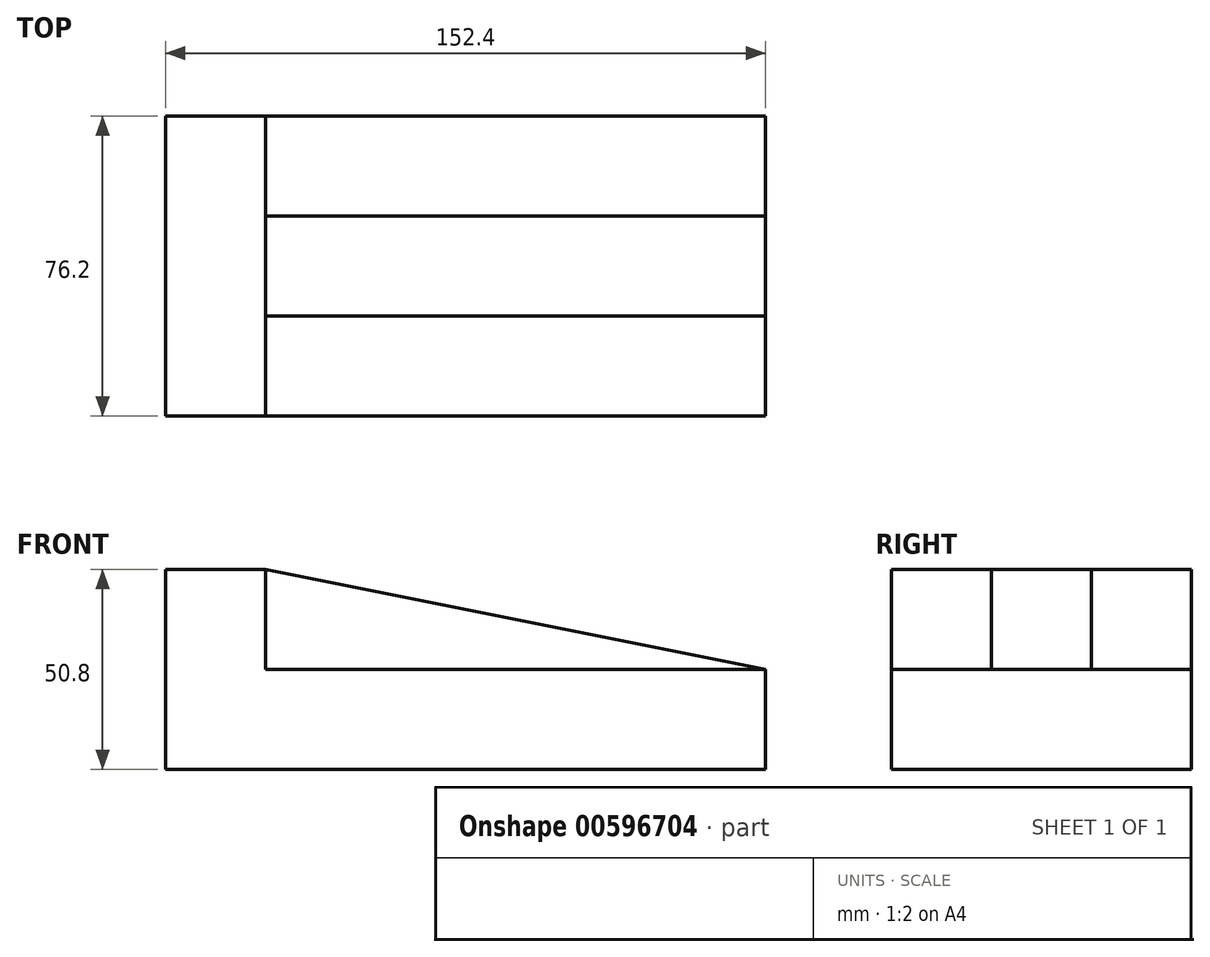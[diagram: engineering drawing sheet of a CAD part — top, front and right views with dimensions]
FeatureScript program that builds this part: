
annotation { "Feature Type Name" : "Feature", "Feature Type Description" : "" }
export const myFeature = defineFeature(function(context is Context, id is Id, definition is map)
    precondition{}
    {
        {
            var Q0;
            Q0=qCreatedBy(makeId("Front.planeOp"),FACE);
            var sketch = newSketch(context, id + "F0", { "sketchPlane" : qUnion([Q0])});
            skLineSegment(sketch, "E0", {"start": v(0, 0) * mm, "end": v(0, 50.8) * mm});
            skLineSegment(sketch, "E1", {"start": v(0, 50.8) * mm, "end": v(25.4, 50.8) * mm});
            skLineSegment(sketch, "E2", {"start": v(0, 0) * mm, "end": v(152.4, 0) * mm});
            skLineSegment(sketch, "E3", {"start": v(152.4, 0) * mm, "end": v(152.4, 25.4) * mm});
            skLineSegment(sketch, "E4", {"start": v(25.4, 50.8) * mm, "end": v(25.4, 25.4) * mm});
            skLineSegment(sketch, "E5", {"start": v(25.4, 25.4) * mm, "end": v(152.4, 25.4) * mm});
            skSolve(sketch);
        }
        {
            var Q0;
            Q0=makeQuery(id+"F0.imprint","IMPRINT",FACE,{"disambiguationData":[TD([[makeQuery(id+"F0.imprint","IMPRINT",EDGE,{"derivedFrom":sQuery(id+"F0.wireOp",EDGE,"E0")}),-1.0]])]});
            extrude(context, id + "F1", {"entities" : qUnion([Q0]), "oppositeDirection" : true, "depth" : 76.2 * mm, "offsetDistance" : 25.4 * mm});
        }
        {
            var Q0;
            Q0=makeQuery(id+"F1.opExtrude","SWEPT_FACE",FACE,{"disambiguationData":[OSD([sQuery(id+"F0.wireOp",EDGE,"E1")])]});
            var sketch = newSketch(context, id + "F2", { "sketchPlane" : qUnion([Q0])});
            skLineSegment(sketch, "E6", {"start": v(25.4, 76.2) * mm, "end": v(25.4, 50.8) * mm});
            skLineSegment(sketch, "E7", {"start": v(25.4, 0) * mm, "end": v(25.4, 25.4) * mm});
            skLineSegment(sketch, "E8", {"start": v(25.4, 25.4) * mm, "end": v(152.4, 25.4) * mm});
            skLineSegment(sketch, "E9", {"start": v(25.4, 50.8) * mm, "end": v(152.4, 50.8) * mm});
            skLineSegment(sketch, "E10", {"start": v(152.4, 50.8) * mm, "end": v(152.4, 25.4) * mm});
            skLineSegment(sketch, "E11", {"start": v(25.4, 50.8) * mm, "end": v(25.4, 25.4) * mm});
            skSolve(sketch);
        }
        {
            var Q0;
            Q0=makeQuery(id+"F2.imprint","IMPRINT",FACE,{"disambiguationData":[TD([[makeQuery(id+"F2.imprint","IMPRINT",EDGE,{"derivedFrom":sQuery(id+"F2.wireOp",EDGE,"E8")}),1.0]])]});
            extrude(context, id + "F3", {"entities" : qUnion([Q0]), "operationType" : NewBodyOperationType.ADD, "oppositeDirection" : true, "depth" : 25.4 * mm, "offsetDistance" : 25.4 * mm});
        }
        {
            var Q0;
            Q0=makeQuery(id+"F3.opExtrude","SWEPT_FACE",FACE,{"disambiguationData":[OSD([sQuery(id+"F2.wireOp",EDGE,"E8")])]});
            var sketch = newSketch(context, id + "F4", { "sketchPlane" : qUnion([Q0])});
            skLineSegment(sketch, "E12", {"start": v(25.4, 50.8) * mm, "end": v(152.4, 25.4) * mm});
            skSolve(sketch);
        }
        {
            var Q0;
            Q0=makeQuery(id+"F4.imprint","IMPRINT",FACE,{"disambiguationData":[TD([[makeQuery(id+"F4.imprint","IMPRINT",EDGE,{"derivedFrom":sQuery(id+"F4.wireOp",EDGE,"E12")}),1.0]])]});
            extrude(context, id + "F5", {"entities" : qUnion([Q0]), "operationType" : NewBodyOperationType.REMOVE, "oppositeDirection" : true, "depth" : 25.4 * mm, "offsetDistance" : 25.4 * mm});
        }
    });
